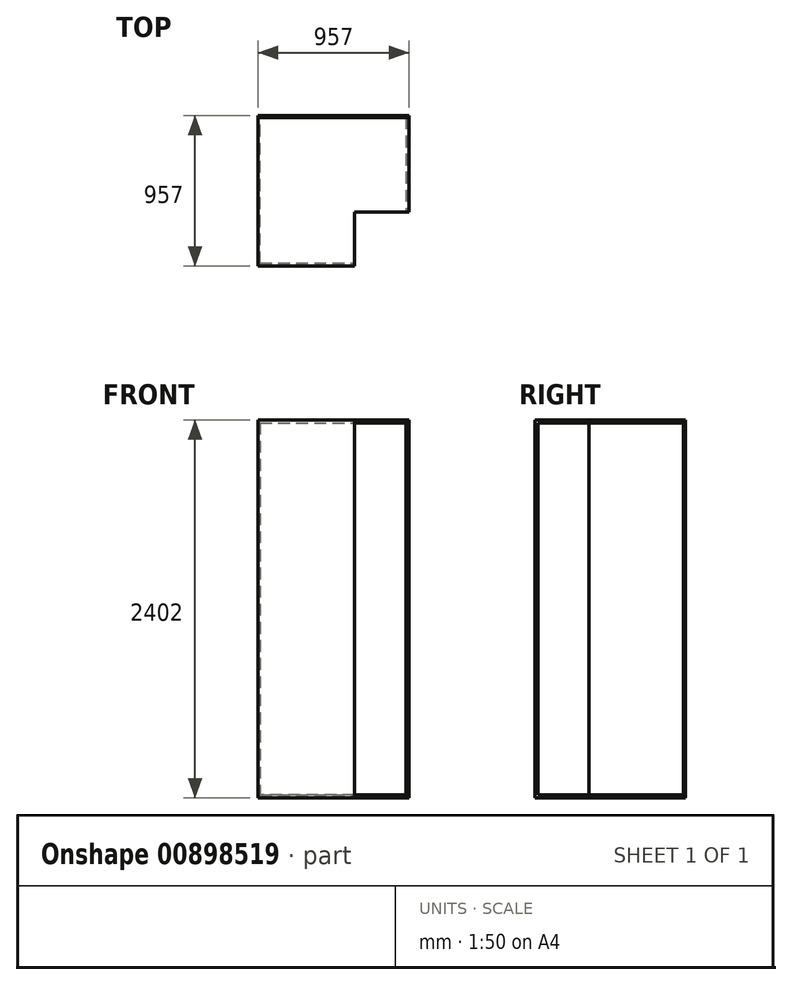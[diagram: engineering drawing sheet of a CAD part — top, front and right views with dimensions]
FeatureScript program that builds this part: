
annotation { "Feature Type Name" : "Feature", "Feature Type Description" : "" }
export const myFeature = defineFeature(function(context is Context, id is Id, definition is map)
    precondition{}
    {
        {
            var Q0;
            Q0=qCreatedBy(makeId("Top.planeOp"),FACE);
            var sketch = newSketch(context, id + "F0", { "sketchPlane" : qUnion([Q0])});
            skLineSegment(sketch, "E0.bottom", {"start": v(472.5, -472.5) * mm, "end": v(-472.5, -472.5) * mm});
            skLineSegment(sketch, "E0.top", {"start": v(472.5, 472.5) * mm, "end": v(-472.5, 472.5) * mm});
            skLineSegment(sketch, "E0.left", {"start": v(472.5, -472.5) * mm, "end": v(472.5, 472.5) * mm});
            skLineSegment(sketch, "E0.right", {"start": v(-472.5, -472.5) * mm, "end": v(-472.5, 472.5) * mm});
            skPoint(sketch, "E0.middle", {"position": v(0, 0) * mm});
            skSolve(sketch);
        }
        {
            assignVariable(context, id + "F1", {"name" : "thickness", "anyValue" : 19});
        }
        {
            var Q0;
            Q0=makeQuery(id+"F0.imprint","IMPRINT",FACE,{"disambiguationData":[TD([[makeQuery(id+"F0.imprint","IMPRINT",EDGE,{"derivedFrom":sQuery(id+"F0.wireOp",EDGE,"E0.bottom")}),-1.0]])]});
            extrude(context, id + "F2", {"entities" : qUnion([Q0]), "depth" : (getVariable(context, 'thickness')) * mm, "offsetDistance" : 25 * mm});
        }
        {
            assignVariable(context, id + "F3", {"name" : "height", "anyValue" : 2364});
        }
        {
            assignVariable(context, id + "F4", {"name" : "back", "anyValue" : 12});
        }
        {
            var Q0;
            Q0=makeQuery(id+"F2.opExtrude","CAP_FACE",FACE,{"disambiguationData":[OSD([sQuery(id+"F0.wireOp",EDGE,"E0.bottom"),sQuery(id+"F0.wireOp",EDGE,"E0.top"),sQuery(id+"F0.wireOp",EDGE,"E0.left"),sQuery(id+"F0.wireOp",EDGE,"E0.right")])],"isStart":false});
            var sketch = newSketch(context, id + "F5", { "sketchPlane" : qUnion([Q0])});
            skLineSegment(sketch, "E1.bottom", {"start": v(472.5, -472.5) * mm, "end": v(127.5, -472.5) * mm});
            skLineSegment(sketch, "E1.top", {"start": v(472.5, -127.5) * mm, "end": v(127.5, -127.5) * mm});
            skLineSegment(sketch, "E1.left", {"start": v(472.5, -472.5) * mm, "end": v(472.5, -127.5) * mm});
            skLineSegment(sketch, "E1.right", {"start": v(127.5, -472.5) * mm, "end": v(127.5, -127.5) * mm});
            skSolve(sketch);
        }
        {
            var Q0;
            Q0=makeQuery(id+"F5.imprint","IMPRINT",FACE,{"disambiguationData":[TD([[makeQuery(id+"F5.imprint","IMPRINT",EDGE,{"derivedFrom":sQuery(id+"F5.wireOp",EDGE,"E1.bottom")}),-1.0]])]});
            extrude(context, id + "F6", {"entities" : qUnion([Q0]), "operationType" : NewBodyOperationType.REMOVE, "endBound" : BoundingType.THROUGH_ALL, "oppositeDirection" : true, "depth" : 25 * mm, "offsetDistance" : 25 * mm});
        }
        {
            var Q0;
            Q0=makeQuery(id+"F2.opExtrude","CAP_FACE",FACE,{"disambiguationData":[OSD([sQuery(id+"F0.wireOp",EDGE,"E0.bottom"),sQuery(id+"F0.wireOp",EDGE,"E0.top"),sQuery(id+"F0.wireOp",EDGE,"E0.left"),sQuery(id+"F0.wireOp",EDGE,"E0.right")])],"isStart":false});
            var sketch = newSketch(context, id + "F7", { "sketchPlane" : qUnion([Q0])});
            skLineSegment(sketch, "E2.bottom", {"start": v(472.5, 472.5) * mm, "end": v(453.5, 472.5) * mm});
            skLineSegment(sketch, "E2.top", {"start": v(472.5, -127.5) * mm, "end": v(453.5, -127.5) * mm});
            skLineSegment(sketch, "E2.left", {"start": v(472.5, 472.5) * mm, "end": v(472.5, -127.5) * mm});
            skLineSegment(sketch, "E2.right", {"start": v(453.5, 472.5) * mm, "end": v(453.5, -127.5) * mm});
            skLineSegment(sketch, "E3.bottom", {"start": v(-472.5, -472.5) * mm, "end": v(127.5, -472.5) * mm});
            skLineSegment(sketch, "E3.top", {"start": v(-472.5, -453.5) * mm, "end": v(127.5, -453.5) * mm});
            skLineSegment(sketch, "E3.left", {"start": v(-472.5, -472.5) * mm, "end": v(-472.5, -453.5) * mm});
            skLineSegment(sketch, "E3.right", {"start": v(127.5, -472.5) * mm, "end": v(127.5, -453.5) * mm});
            skSolve(sketch);
        }
        {
            var Q0;
            Q0=makeQuery(id+"F7.imprint","IMPRINT",FACE,{"disambiguationData":[TD([[makeQuery(id+"F7.imprint","IMPRINT",EDGE,{"derivedFrom":sQuery(id+"F7.wireOp",EDGE,"E3.bottom")}),-1.0]])]});
            extrude(context, id + "F8", {"entities" : qUnion([Q0]), "depth" : (getVariable(context, 'height')) * mm, "offsetDistance" : 25 * mm});
        }
        {
            var Q0;
            Q0=makeQuery(id+"F7.imprint","IMPRINT",FACE,{"disambiguationData":[TD([[makeQuery(id+"F7.imprint","IMPRINT",EDGE,{"derivedFrom":sQuery(id+"F7.wireOp",EDGE,"E2.bottom")}),1.0]])]});
            extrude(context, id + "F9", {"entities" : qUnion([Q0]), "depth" : (getVariable(context, 'height')) * mm, "offsetDistance" : 25 * mm});
        }
        {
            var Q0;
            Q0=makeQuery(id+"F8.opExtrude","CAP_FACE",FACE,{"disambiguationData":[OSD([sQuery(id+"F7.wireOp",EDGE,"E3.bottom"),sQuery(id+"F7.wireOp",EDGE,"E3.top"),sQuery(id+"F7.wireOp",EDGE,"E3.left"),sQuery(id+"F7.wireOp",EDGE,"E3.right")])],"isStart":false});
            var sketch = newSketch(context, id + "F10", { "sketchPlane" : qUnion([Q0])});
            skLineSegment(sketch, "E4.bottom", {"start": v(-472.5, -472.5) * mm, "end": v(472.5, -472.5) * mm});
            skLineSegment(sketch, "E4.top", {"start": v(-472.5, 472.5) * mm, "end": v(472.5, 472.5) * mm});
            skLineSegment(sketch, "E4.left", {"start": v(-472.5, -472.5) * mm, "end": v(-472.5, 472.5) * mm});
            skLineSegment(sketch, "E4.right", {"start": v(472.5, -472.5) * mm, "end": v(472.5, 472.5) * mm});
            skLineSegment(sketch, "E5.bottom", {"start": v(472.5, -472.5) * mm, "end": v(127.5, -472.5) * mm});
            skLineSegment(sketch, "E5.top", {"start": v(472.5, -127.5) * mm, "end": v(127.5, -127.5) * mm});
            skLineSegment(sketch, "E5.left", {"start": v(472.5, -472.5) * mm, "end": v(472.5, -127.5) * mm});
            skLineSegment(sketch, "E5.right", {"start": v(127.5, -472.5) * mm, "end": v(127.5, -127.5) * mm});
            skSolve(sketch);
        }
        {
            var Q0;
            {var subQ2=sQuery(id+"F10.wireOp",EDGE,"E4.top");Q0=makeQuery(id+"F10.imprint","IMPRINT",FACE,{"disambiguationData":[TD([[makeQuery(id+"F10.imprint","IMPRINT",EDGE,{"derivedFrom":subQ2}),-1.0]])]});}
            var Q1;
            {var subQ0=sQuery(id+"F10.wireOp",EDGE,"E4.bottom");Q1=makeQuery(id+"F10.imprint","IMPRINT",FACE,{"disambiguationData":[TD([[makeQuery(id+"F10.imprint","IMPRINT",EDGE,{"derivedFrom":subQ0}),-1.0]])]});}
            extrude(context, id + "F11", {"entities" : qUnion([Q0, Q1]), "depth" : (getVariable(context, 'thickness')) * mm, "offsetDistance" : 25 * mm});
        }
        {
            var Q0;
            Q0=makeQuery(id+"F11.opExtrude","SWEPT_FACE",FACE,{"disambiguationData":[OSD([sQuery(id+"F10.wireOp",EDGE,"E4.left")])]});
            var sketch = newSketch(context, id + "F12", { "sketchPlane" : qUnion([Q0])});
            skLineSegment(sketch, "E6.bottom", {"start": v(472.5, 2402) * mm, "end": v(-472.5, 2402) * mm});
            skLineSegment(sketch, "E6.top", {"start": v(472.5, 0) * mm, "end": v(-472.5, 0) * mm});
            skLineSegment(sketch, "E6.left", {"start": v(472.5, 2402) * mm, "end": v(472.5, 0) * mm});
            skLineSegment(sketch, "E6.right", {"start": v(-472.5, 2402) * mm, "end": v(-472.5, 0) * mm});
            skSolve(sketch);
        }
        {
            var Q0;
            {var subQ0=sQuery(id+"F12.wireOp",EDGE,"E6.top");Q0=makeQuery(id+"F12.imprint","IMPRINT",FACE,{"disambiguationData":[TD([[makeQuery(id+"F12.imprint","IMPRINT",EDGE,{"derivedFrom":subQ0}),-1.0]])]});}
            var Q1;
            {var subQ0=sQuery(id+"F12.wireOp",EDGE,"E6.bottom");Q1=makeQuery(id+"F12.imprint","IMPRINT",FACE,{"disambiguationData":[TD([[makeQuery(id+"F12.imprint","IMPRINT",EDGE,{"derivedFrom":subQ0}),1.0]])]});}
            extrude(context, id + "F13", {"entities" : qUnion([Q0, Q1]), "operationType" : NewBodyOperationType.ADD, "depth" : (getVariable(context, 'back')) * mm, "offsetDistance" : 25 * mm});
        }
        {
            var Q0;
            Q0=makeQuery(id+"F11.opExtrude","SWEPT_FACE",FACE,{"disambiguationData":[OSD([sQuery(id+"F10.wireOp",EDGE,"E4.top")])]});
            var sketch = newSketch(context, id + "F14", { "sketchPlane" : qUnion([Q0])});
            skLineSegment(sketch, "E7.bottom", {"start": v(-472.5, 2402) * mm, "end": v(484.5, 2402) * mm});
            skLineSegment(sketch, "E7.top", {"start": v(-472.5, 0) * mm, "end": v(484.5, 0) * mm});
            skLineSegment(sketch, "E7.left", {"start": v(-472.5, 2402) * mm, "end": v(-472.5, 0) * mm});
            skLineSegment(sketch, "E7.right", {"start": v(484.5, 2402) * mm, "end": v(484.5, 0) * mm});
            skSolve(sketch);
        }
        {
            var Q0;
            {var subQ4=sQuery(id+"F14.wireOp",EDGE,"E7.top");Q0=makeQuery(id+"F14.imprint","IMPRINT",FACE,{"disambiguationData":[TD([[makeQuery(id+"F14.imprint","IMPRINT",EDGE,{"derivedFrom":subQ4}),1.0]])]});}
            var Q1;
            {var subQ1=sQuery(id+"F10.wireOp",EDGE,"E4.top");var subQ5=makeQuery(id+"F11.opExtrude","CAP_EDGE",EDGE,{"disambiguationData":[OSD([subQ1])],"isStart":true});Q1=makeQuery(id+"F14.imprint","IMPRINT",FACE,{"disambiguationData":[TD([[makeQuery(id+"F14.imprint","IMPRINT",EDGE,{"derivedFrom":subQ5}),-1.0]])]});}
            extrude(context, id + "F15", {"entities" : qUnion([Q0, Q1]), "depth" : (getVariable(context, 'back')) * mm, "offsetDistance" : 25 * mm});
        }
    });
